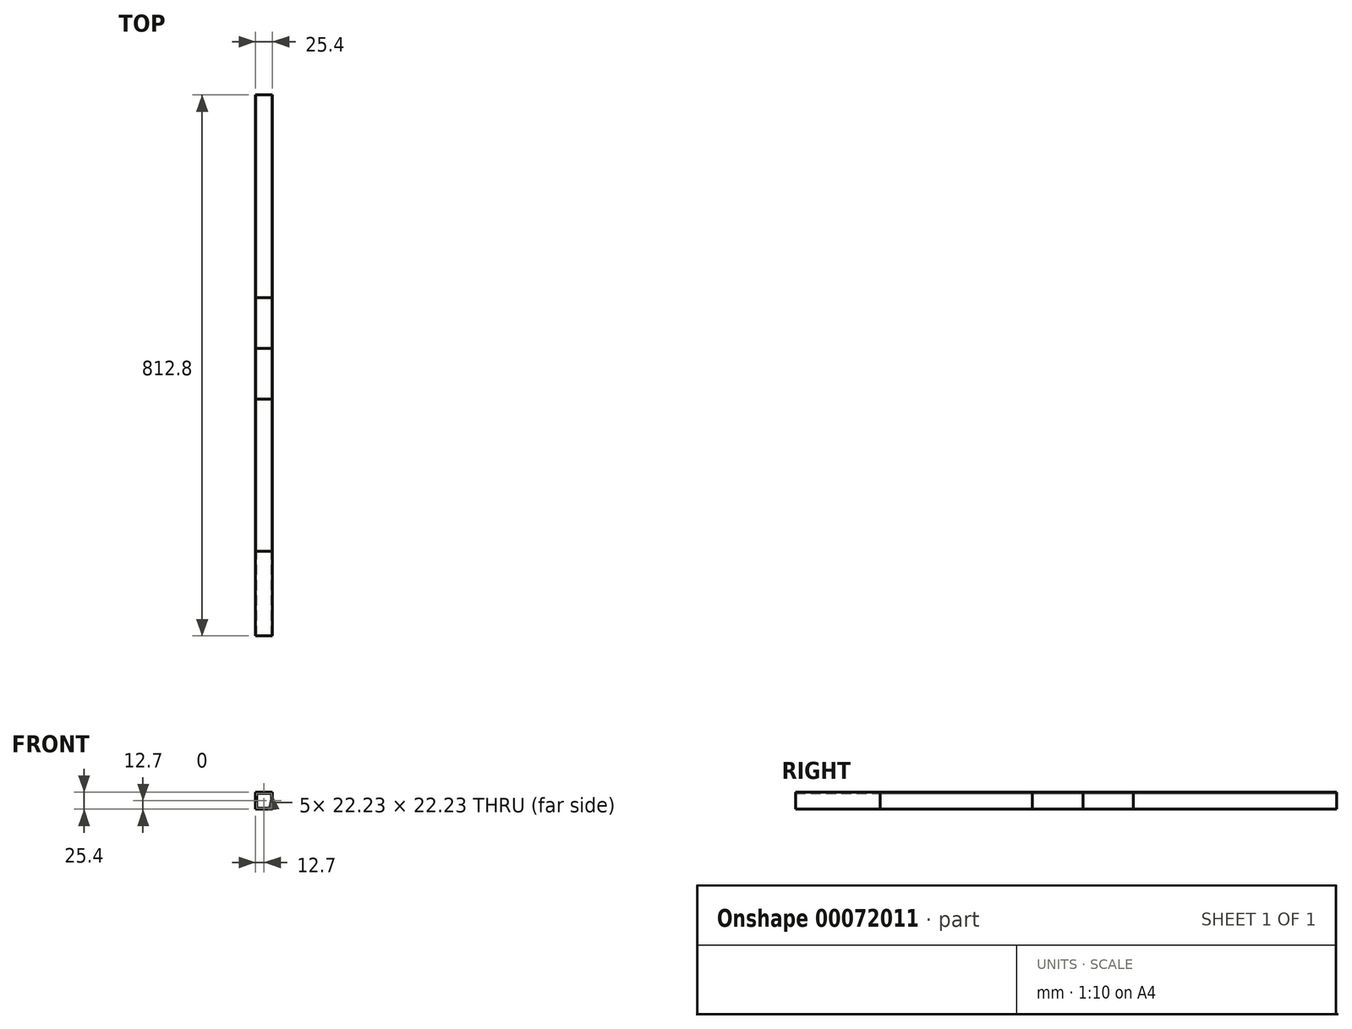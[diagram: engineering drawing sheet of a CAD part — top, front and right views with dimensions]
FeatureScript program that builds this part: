
annotation { "Feature Type Name" : "Feature", "Feature Type Description" : "" }
export const myFeature = defineFeature(function(context is Context, id is Id, definition is map)
    precondition{}
    {
        {
            var Q0;
            Q0=qCreatedBy(makeId("Front.planeOp"),FACE);
            var sketch = newSketch(context, id + "F0", { "sketchPlane" : qUnion([Q0])});
            skLineSegment(sketch, "E0.bottom", {"start": v(0, 0) * mm, "end": v(25.4, 0) * mm});
            skLineSegment(sketch, "E0.top", {"start": v(0, 25.4) * mm, "end": v(25.4, 25.4) * mm});
            skLineSegment(sketch, "E0.left", {"start": v(0, 0) * mm, "end": v(0, 25.4) * mm});
            skLineSegment(sketch, "E0.right", {"start": v(25.4, 0) * mm, "end": v(25.4, 25.4) * mm});
            skLineSegment(sketch, "E1.bottom", {"start": v(1.59, 1.59) * mm, "end": v(23.81, 1.59) * mm});
            skLineSegment(sketch, "E1.top", {"start": v(1.59, 23.81) * mm, "end": v(23.81, 23.81) * mm});
            skLineSegment(sketch, "E1.left", {"start": v(1.59, 1.59) * mm, "end": v(1.59, 23.81) * mm});
            skLineSegment(sketch, "E1.right", {"start": v(23.81, 1.59) * mm, "end": v(23.81, 23.81) * mm});
            skSolve(sketch);
        }
        {
            var Q0;
            Q0=qSketchRegion(id+"F0",true);
            extrude(context, id + "F1", {"entities" : qUnion([Q0]), "depth" : 304.8 * mm});
        }
        {
            var Q0;
            Q0=qSketchRegion(id+"F0",true);
            extrude(context, id + "F2", {"entities" : qUnion([Q0]), "depth" : 812.8 * mm});
        }
        {
            var Q0;
            Q0=qSketchRegion(id+"F0",true);
            extrude(context, id + "F3", {"entities" : qUnion([Q0]), "depth" : 685.8 * mm});
        }
        {
            var Q0;
            Q0=qSketchRegion(id+"F0",true);
            extrude(context, id + "F4", {"entities" : qUnion([Q0]), "depth" : 457.2 * mm});
        }
        {
            var Q0;
            Q0=qSketchRegion(id+"F0",true);
            extrude(context, id + "F5", {"entities" : qUnion([Q0]), "depth" : 381 * mm});
        }
    });
